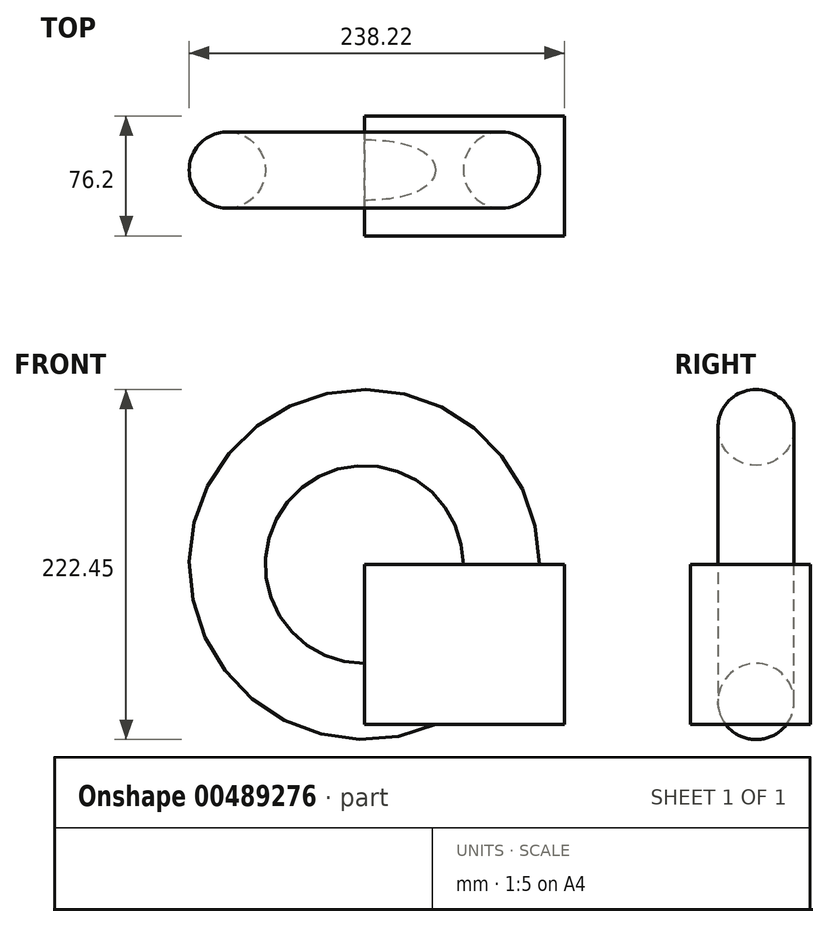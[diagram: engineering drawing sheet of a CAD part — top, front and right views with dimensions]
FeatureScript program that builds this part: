
annotation { "Feature Type Name" : "Feature", "Feature Type Description" : "" }
export const myFeature = defineFeature(function(context is Context, id is Id, definition is map)
    precondition{}
    {
        {
            var Q0;
            Q0=qCreatedBy(makeId("Front.planeOp"),FACE);
            var sketch = newSketch(context, id + "F0", { "sketchPlane" : qUnion([Q0])});
            skLineSegment(sketch, "E0.bottom", {"start": v(-94.8, 54.93) * mm, "end": v(32.2, 54.93) * mm});
            skLineSegment(sketch, "E0.top", {"start": v(-94.8, -46.67) * mm, "end": v(32.2, -46.67) * mm});
            skLineSegment(sketch, "E0.left", {"start": v(-94.8, 54.93) * mm, "end": v(-94.8, -46.67) * mm});
            skLineSegment(sketch, "E0.right", {"start": v(32.2, 54.93) * mm, "end": v(32.2, -46.67) * mm});
            skSolve(sketch);
        }
        {
            var Q0;
            Q0 = qSketchRegion(id + "F0", true);
            extrude(context, id + "F1", {"entities" : qUnion([Q0]), "depth" : 76.2 * mm, "hasDraft" : true, "draftAngle" : 0 * degree});
        }
        {
            var Q0;
            Q0=makeQuery(id+"F1.opExtrude","SWEPT_FACE",FACE,{"disambiguationData":[OSD([sQuery(id+"F0.wireOp",EDGE,"E0.bottom")])]});
            var sketch = newSketch(context, id + "F2", { "sketchPlane" : qUnion([Q0])});
            skCircle(sketch, "E1", {"center": v(-7.76, -34.37) * mm, "radius": 24.18 * mm});
            skSolve(sketch);
        }
        {
            var Q0;
            Q0=makeQuery(id+"F2.imprint","IMPRINT",FACE,{"disambiguationData":[TD([[makeQuery(id+"F2.imprint","IMPRINT",EDGE,{"derivedFrom":sQuery(id+"F2.wireOp",EDGE,"E1")}),1.0]])]});
            var Q1;
            Q1=makeQuery(id+"F1.opExtrude","SWEPT_EDGE",EDGE,{"disambiguationData":[OSD([sQuery(id+"F0.wireOp",EDGE,"E0.bottom"),sQuery(id+"F0.wireOp",EDGE,"E0.left")])]});
            revolve(context, id + "F3", {"operationType" : NewBodyOperationType.ADD, "entities" : qUnion([Q0]), "axis" : qUnion([Q1]), "revolveType" : RevolveType.FULL});
        }
    });
